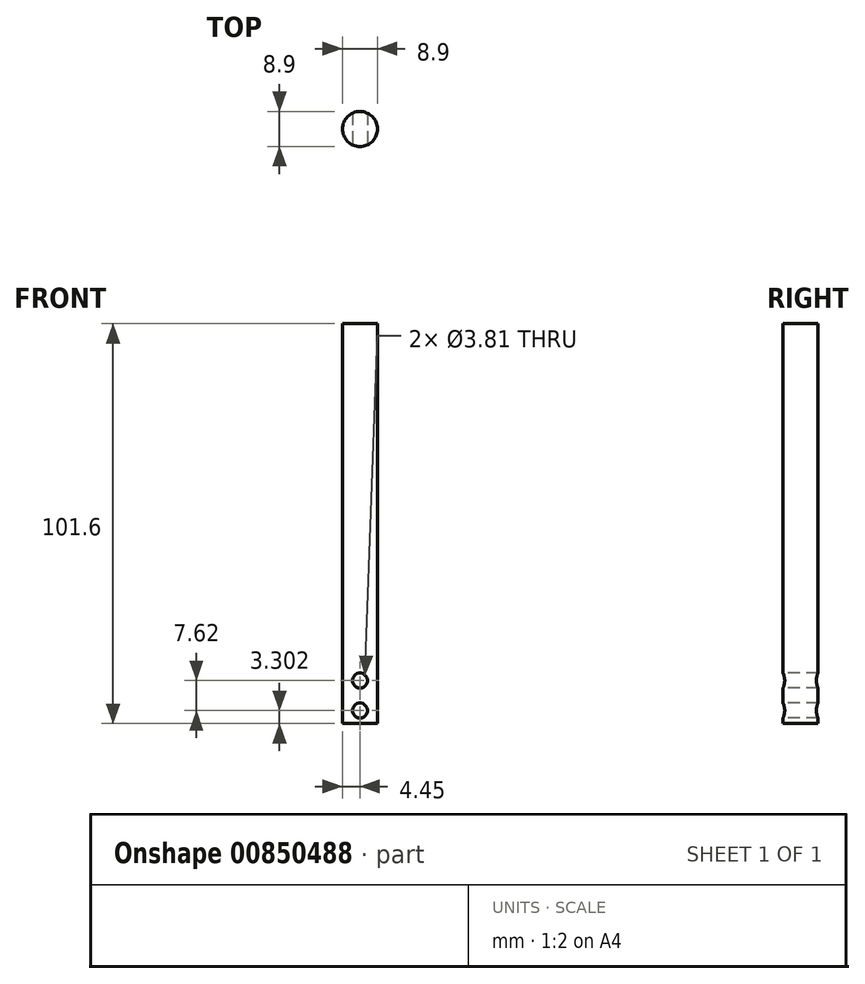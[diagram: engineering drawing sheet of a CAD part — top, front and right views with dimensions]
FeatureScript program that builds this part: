
annotation { "Feature Type Name" : "Feature", "Feature Type Description" : "" }
export const myFeature = defineFeature(function(context is Context, id is Id, definition is map)
    precondition{}
    {
        {
            var Q0;
            Q0=qCreatedBy(makeId("Top.planeOp"),FACE);
            var sketch = newSketch(context, id + "F0", { "sketchPlane" : qUnion([Q0])});
            skCircle(sketch, "E0", {"center": v(0, 0) * mm, "radius": 4.45 * mm});
            skSolve(sketch);
        }
        {
            var Q0;
            Q0 = qSketchRegion(id + "F0", true);
            extrude(context, id + "F1", {"entities" : qUnion([Q0]), "depth" : 101.6 * mm, "offsetDistance" : 25.4 * mm});
        }
        {
            var Q0;
            Q0=qCreatedBy(makeId("Front.planeOp"),FACE);
            var sketch = newSketch(context, id + "F2", { "sketchPlane" : qUnion([Q0])});
            skCircle(sketch, "E1", {"center": v(0, 3.3) * mm, "radius": 1.9 * mm});
            skCircle(sketch, "E2", {"center": v(0, 10.92) * mm, "radius": 1.9 * mm});
            skSolve(sketch);
        }
        {
            var Q0;
            Q0 = qSketchRegion(id + "F2", true);
            extrude(context, id + "F3", {"entities" : qUnion([Q0]), "operationType" : NewBodyOperationType.REMOVE, "endBound" : BoundingType.THROUGH_ALL, "oppositeDirection" : true, "depth" : 25.4 * mm, "offsetDistance" : 25.4 * mm, "hasSecondDirection" : true, "secondDirectionOppositeDirection" : false, "secondDirectionDepth" : 12.7 * mm});
        }
    });
